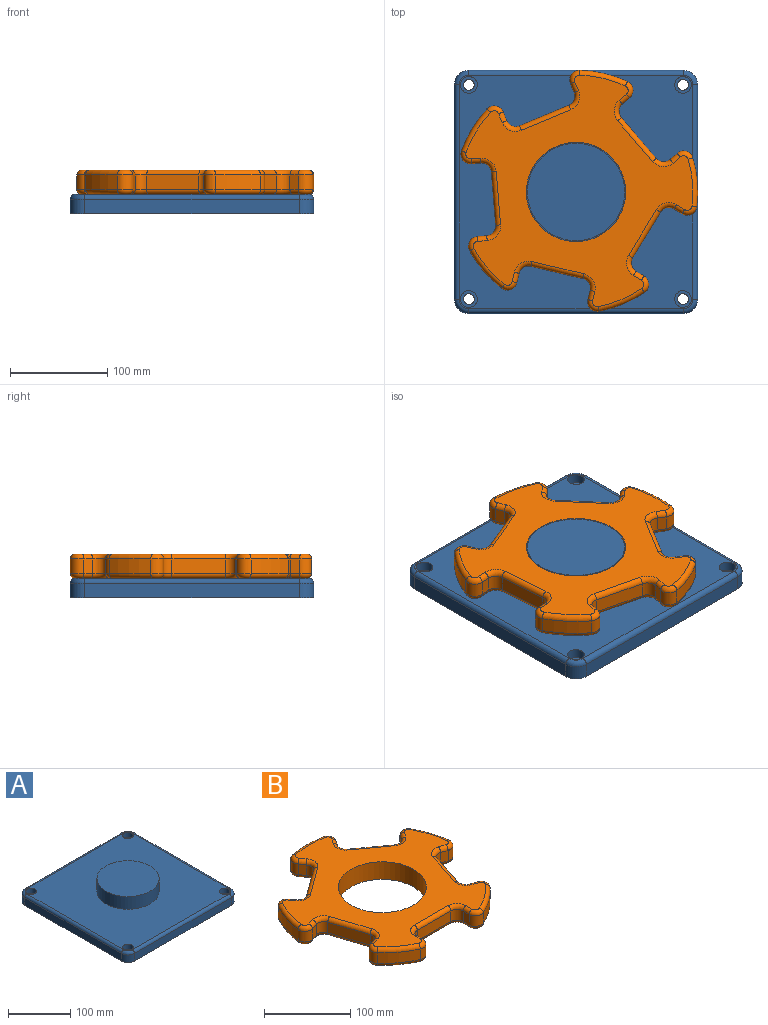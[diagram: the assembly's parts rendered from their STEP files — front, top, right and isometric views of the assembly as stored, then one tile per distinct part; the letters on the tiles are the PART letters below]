
ASSEMBLY  parts=2 mates=1
PART A: 32 faces, bbox 252.5x252.5x45 mm
  f0: plane 220x15mm, normal (1,0,0), area 3300mm2, adj f5,f8,f11,f27
  f1: plane 220x15mm, normal (0,1,0), area 3300mm2, adj f5,f8,f9,f31
  f2: plane 220x15mm, normal (-1,0,0), area 3300mm2, adj f5,f9,f10,f28
  f3: plane 220x15mm, normal (0,-1,0), area 3300mm2, adj f5,f10,f11,f24
  f4: plane 240x240mm, normal (0,0,1), area 48725.4mm2, adj f6,f14,f17,f20,f23,f24,f25,f26
  f5: plane 250x250mm, normal (0,0,-1), area 61926.7mm2, adj f0,f1,f2,f3,f8,f9,f10,f11
  f6: cylinder r=50mm len=100mm, axis (0,0,-1), area 7854mm2, adj f4,f7
  f7: plane 100x100mm, normal (0,0,1), area 7854mm2, adj f6
  f8: cylinder r=15mm len=15mm, axis (0,0,-1), area 353.4mm2, adj f0,f1,f5,f29
  f9: cylinder r=15mm len=15mm, axis (0,0,1), area 353.4mm2, adj f1,f2,f5,f30
  f10: cylinder r=15mm len=15mm, axis (0,0,-1), area 353.4mm2, adj f2,f3,f5,f26
  f11: cylinder r=15mm len=15mm, axis (0,0,1), area 353.4mm2, adj f0,f3,f5,f25
  f12: cylinder r=5.5mm len=11mm, axis (0,0,1), area 345.6mm2, adj f5,f13
  f13: plane 17.25x17.25mm, normal (0,0,1), area 138.7mm2, adj f12,f14
  f14: cylinder r=8.62mm len=17.25mm, axis (0,0,1), area 541.9mm2, adj f4,f13
  f15: cylinder r=5.5mm len=11mm, axis (0,0,1), area 345.6mm2, adj f5,f16
  f16: plane 17.25x17.25mm, normal (0,0,1), area 138.7mm2, adj f15,f17
  f17: cylinder r=8.62mm len=17.25mm, axis (0,0,1), area 541.9mm2, adj f4,f16
  f18: cylinder r=5.5mm len=11mm, axis (0,0,1), area 345.6mm2, adj f5,f19
  f19: plane 17.25x17.25mm, normal (0,0,1), area 138.7mm2, adj f18,f20
  f20: cylinder r=8.62mm len=17.25mm, axis (0,0,1), area 541.9mm2, adj f4,f19
  f21: cylinder r=5.5mm len=11mm, axis (0,0,1), area 345.6mm2, adj f5,f22
  f22: plane 17.25x17.25mm, normal (0,0,1), area 138.7mm2, adj f21,f23
  f23: cylinder r=8.62mm len=17.25mm, axis (0,0,1), area 541.9mm2, adj f4,f22
  f24: cylinder r=5mm len=220mm, axis (-1,0,0), area 1727.9mm2, adj f3,f4,f25,f26
  f25: torus R=10mm, axis (0,0,1), area 162.6mm2, adj f4,f11,f24,f27
  f26: torus R=10mm, axis (0,0,1), area 162.6mm2, adj f4,f10,f24,f28
  f27: cylinder r=5mm len=220mm, axis (0,-1,0), area 1727.9mm2, adj f0,f4,f25,f29
  f28: cylinder r=5mm len=220mm, axis (0,1,0), area 1727.9mm2, adj f2,f4,f26,f30
  f29: torus R=10mm, axis (0,0,1), area 162.6mm2, adj f4,f8,f27,f31
  f30: torus R=10mm, axis (0,0,1), area 162.6mm2, adj f4,f9,f28,f31
  f31: cylinder r=5mm len=220mm, axis (1,0,0), area 1727.9mm2, adj f1,f4,f29,f30
PART B: 123 faces, bbox 268.9x258.5x25 mm
  f0: plane 238.57x229.73mm, normal (0,0,1), area 21505.7mm2, adj f6,f43,f44,f45,f46,f47,f48,f49
  f1: plane 238.57x229.73mm, normal (0,0,-1), area 21505.7mm2, adj f6,f83,f84,f85,f86,f87,f88,f89
  f2: cylinder r=125mm len=40.68mm, axis (0,0,-1), area 759.5mm2, adj f13,f42,f51,f91
  f3: cylinder r=125mm len=47.82mm, axis (0,0,-1), area 759.5mm2, adj f35,f41,f67,f107
  f4: cylinder r=125mm len=50.29mm, axis (0,0,-1), area 759.5mm2, adj f28,f34,f82,f122
  f5: cylinder r=125mm len=47.82mm, axis (0,0,-1), area 759.5mm2, adj f21,f27,f66,f106
  f6: cylinder r=51mm len=102mm, axis (0,0,-1), area 8011.1mm2, adj f0,f1
  f7: cylinder r=125mm len=40.68mm, axis (0,0,-1), area 759.5mm2, adj f14,f20,f50,f90
  f8: plane 15x9.73mm, normal (-1,0,0), area 146mm2, adj f11,f14,f46,f86
  f9: plane 55x15mm, normal (0,-1,0), area 825mm2, adj f11,f12,f43,f83
  f10: plane 15x9.73mm, normal (1,0,0), area 146mm2, adj f12,f13,f47,f87
  f11: cylinder r=10mm len=15mm, axis (0,0,-1), area 235.6mm2, adj f8,f9,f44,f84
  f12: cylinder r=10mm len=15mm, axis (0,0,-1), area 235.6mm2, adj f9,f10,f45,f85
  f13: cylinder r=10mm len=15mm, axis (0,0,-1), area 299.5mm2, adj f2,f10,f49,f89
  f14: cylinder r=10mm len=15mm, axis (0,0,-1), area 299.5mm2, adj f7,f8,f48,f88
  f15: plane 15x9.26mm, normal (-0.31,-0.95,0), area 146mm2, adj f18,f21,f62,f102
  f16: plane 52.31x17mm, normal (0.95,-0.31,0), area 825mm2, adj f18,f19,f58,f98
  f17: plane 15x9.26mm, normal (0.31,0.95,0), area 146mm2, adj f19,f20,f54,f94
  f18: cylinder r=10mm len=15mm, axis (0,0,-1), area 235.6mm2, adj f15,f16,f60,f100
  f19: cylinder r=10mm len=15mm, axis (0,0,-1), area 235.6mm2, adj f16,f17,f56,f96
  f20: cylinder r=10mm len=16.25mm, axis (0,0,-1), area 299.5mm2, adj f7,f17,f52,f92
  f21: cylinder r=10mm len=15mm, axis (0,0,-1), area 299.5mm2, adj f5,f15,f64,f104
  f22: plane 15x7.87mm, normal (0.81,-0.59,0), area 146mm2, adj f25,f28,f78,f118
  f23: plane 44.5x32.33mm, normal (0.59,0.81,0), area 825mm2, adj f25,f26,f74,f114
  f24: plane 15x7.87mm, normal (-0.81,0.59,0), area 146mm2, adj f26,f27,f70,f110
  f25: cylinder r=10mm len=15mm, axis (0,0,-1), area 235.6mm2, adj f22,f23,f76,f116
  f26: cylinder r=10mm len=15mm, axis (0,0,-1), area 235.6mm2, adj f23,f24,f72,f112
  f27: cylinder r=10mm len=16.78mm, axis (0,0,-1), area 299.5mm2, adj f5,f24,f68,f108
  f28: cylinder r=10mm len=15.67mm, axis (0,0,-1), area 299.5mm2, adj f4,f22,f80,f120
  f29: plane 15x7.87mm, normal (0.81,0.59,0), area 146mm2, adj f32,f35,f71,f111
  f30: plane 44.5x32.33mm, normal (-0.59,0.81,0), area 825mm2, adj f32,f33,f75,f115
  f31: plane 15x7.87mm, normal (-0.81,-0.59,0), area 146mm2, adj f33,f34,f79,f119
  f32: cylinder r=10mm len=15mm, axis (0,0,-1), area 235.6mm2, adj f29,f30,f73,f113
  f33: cylinder r=10mm len=15mm, axis (0,0,-1), area 235.6mm2, adj f30,f31,f77,f117
  f34: cylinder r=10mm len=15.67mm, axis (0,0,-1), area 299.5mm2, adj f4,f31,f81,f121
  f35: cylinder r=10mm len=16.78mm, axis (0,0,-1), area 299.5mm2, adj f3,f29,f69,f109
  f36: plane 15x9.26mm, normal (-0.31,0.95,0), area 146mm2, adj f39,f42,f55,f95
  f37: plane 52.31x17mm, normal (-0.95,-0.31,0), area 825mm2, adj f39,f40,f59,f99
  f38: plane 15x9.26mm, normal (0.31,-0.95,0), area 146mm2, adj f40,f41,f63,f103
  f39: cylinder r=10mm len=15mm, axis (0,0,-1), area 235.6mm2, adj f36,f37,f57,f97
  f40: cylinder r=10mm len=15mm, axis (0,0,-1), area 235.6mm2, adj f37,f38,f61,f101
  f41: cylinder r=10mm len=15mm, axis (0,0,-1), area 299.5mm2, adj f3,f38,f65,f105
  f42: cylinder r=10mm len=16.25mm, axis (0,0,-1), area 299.5mm2, adj f2,f36,f53,f93
  f43: cylinder r=5mm len=55mm, axis (1,0,0), area 432mm2, adj f0,f9,f44,f45
  f44: torus R=15mm, axis (0,0,1), area 145.8mm2, adj f0,f11,f43,f46
  f45: torus R=15mm, axis (0,0,1), area 145.8mm2, adj f0,f12,f43,f47
  f46: cylinder r=5mm len=9.73mm, axis (0,-1,0), area 76.4mm2, adj f0,f8,f44,f48
  f47: cylinder r=5mm len=9.73mm, axis (0,1,0), area 76.4mm2, adj f0,f10,f45,f49
  f48: torus R=5mm, axis (0,0,1), area 128.3mm2, adj f0,f14,f46,f50
  f49: torus R=5mm, axis (0,0,1), area 128.3mm2, adj f0,f13,f47,f51
  f50: torus R=120mm, axis (0,0,1), area 391.9mm2, adj f0,f7,f48,f52
  f51: torus R=120mm, axis (0,0,1), area 391.9mm2, adj f0,f2,f49,f53
  f52: torus R=5mm, axis (0,0,1), area 128.3mm2, adj f0,f20,f50,f54
  f53: torus R=5mm, axis (0,0,1), area 128.3mm2, adj f0,f42,f51,f55
  f54: cylinder r=5mm len=10.8mm, axis (-0.95,0.31,0), area 76.4mm2, adj f0,f17,f52,f56
  f55: cylinder r=5mm len=10.8mm, axis (-0.95,-0.31,0), area 76.4mm2, adj f0,f36,f53,f57
  f56: torus R=15mm, axis (0,0,1), area 145.8mm2, adj f0,f19,f54,f58
  f57: torus R=15mm, axis (0,0,1), area 145.8mm2, adj f0,f39,f55,f59
  f58: cylinder r=5mm len=53.85mm, axis (0.31,0.95,0), area 432mm2, adj f0,f16,f56,f60
  f59: cylinder r=5mm len=53.85mm, axis (0.31,-0.95,0), area 432mm2, adj f0,f37,f57,f61
  f60: torus R=15mm, axis (0,0,1), area 145.8mm2, adj f0,f18,f58,f62
  f61: torus R=15mm, axis (0,0,1), area 145.8mm2, adj f0,f40,f59,f63
  f62: cylinder r=5mm len=10.8mm, axis (0.95,-0.31,0), area 76.4mm2, adj f0,f15,f60,f64
  f63: cylinder r=5mm len=10.8mm, axis (0.95,0.31,0), area 76.4mm2, adj f0,f38,f61,f65
  f64: torus R=5mm, axis (0,0,1), area 128.3mm2, adj f0,f21,f62,f66
  f65: torus R=5mm, axis (0,0,1), area 128.3mm2, adj f0,f41,f63,f67
  f66: torus R=120mm, axis (0,0,1), area 391.9mm2, adj f0,f5,f64,f68
  f67: torus R=120mm, axis (0,0,1), area 391.9mm2, adj f0,f3,f65,f69
  f68: torus R=5mm, axis (0,0,1), area 128.3mm2, adj f0,f27,f66,f70
  f69: torus R=5mm, axis (0,0,1), area 128.3mm2, adj f0,f35,f67,f71
  f70: cylinder r=5mm len=10.81mm, axis (-0.59,-0.81,0), area 76.4mm2, adj f0,f24,f68,f72
  f71: cylinder r=5mm len=10.81mm, axis (-0.59,0.81,0), area 76.4mm2, adj f0,f29,f69,f73
  f72: torus R=15mm, axis (0,0,1), area 145.8mm2, adj f0,f26,f70,f74
  f73: torus R=15mm, axis (0,0,1), area 145.8mm2, adj f0,f32,f71,f75
  f74: cylinder r=5mm len=47.44mm, axis (-0.81,0.59,0), area 432mm2, adj f0,f23,f72,f76
  f75: cylinder r=5mm len=47.44mm, axis (-0.81,-0.59,0), area 432mm2, adj f0,f30,f73,f77
  f76: torus R=15mm, axis (0,0,1), area 145.8mm2, adj f0,f25,f74,f78
  f77: torus R=15mm, axis (0,0,1), area 145.8mm2, adj f0,f33,f75,f79
  f78: cylinder r=5mm len=10.81mm, axis (0.59,0.81,0), area 76.4mm2, adj f0,f22,f76,f80
  f79: cylinder r=5mm len=10.81mm, axis (0.59,-0.81,0), area 76.4mm2, adj f0,f31,f77,f81
  f80: torus R=5mm, axis (0,0,1), area 128.3mm2, adj f0,f28,f78,f82
  f81: torus R=5mm, axis (0,0,1), area 128.3mm2, adj f0,f34,f79,f82
  f82: torus R=120mm, axis (0,0,1), area 391.9mm2, adj f0,f4,f80,f81
  f83: cylinder r=5mm len=55mm, axis (-1,0,0), area 432mm2, adj f1,f9,f84,f85
  f84: torus R=15mm, axis (0,0,1), area 145.8mm2, adj f1,f11,f83,f86
  f85: torus R=15mm, axis (0,0,1), area 145.8mm2, adj f1,f12,f83,f87
  f86: cylinder r=5mm len=9.73mm, axis (0,1,0), area 76.4mm2, adj f1,f8,f84,f88
  f87: cylinder r=5mm len=9.73mm, axis (0,-1,0), area 76.4mm2, adj f1,f10,f85,f89
  f88: torus R=5mm, axis (0,0,1), area 128.3mm2, adj f1,f14,f86,f90
  f89: torus R=5mm, axis (0,0,1), area 128.3mm2, adj f1,f13,f87,f91
  f90: torus R=120mm, axis (0,0,1), area 391.9mm2, adj f1,f7,f88,f92
  f91: torus R=120mm, axis (0,0,1), area 391.9mm2, adj f1,f2,f89,f93
  f92: torus R=5mm, axis (0,0,1), area 128.3mm2, adj f1,f20,f90,f94
  f93: torus R=5mm, axis (0,0,1), area 128.3mm2, adj f1,f42,f91,f95
  f94: cylinder r=5mm len=10.8mm, axis (0.95,-0.31,0), area 76.4mm2, adj f1,f17,f92,f96
  f95: cylinder r=5mm len=10.8mm, axis (0.95,0.31,0), area 76.4mm2, adj f1,f36,f93,f97
  f96: torus R=15mm, axis (0,0,1), area 145.8mm2, adj f1,f19,f94,f98
  f97: torus R=15mm, axis (0,0,1), area 145.8mm2, adj f1,f39,f95,f99
  f98: cylinder r=5mm len=53.85mm, axis (-0.31,-0.95,0), area 432mm2, adj f1,f16,f96,f100
  f99: cylinder r=5mm len=53.85mm, axis (-0.31,0.95,0), area 432mm2, adj f1,f37,f97,f101
  f100: torus R=15mm, axis (0,0,1), area 145.8mm2, adj f1,f18,f98,f102
  f101: torus R=15mm, axis (0,0,1), area 145.8mm2, adj f1,f40,f99,f103
  f102: cylinder r=5mm len=10.8mm, axis (-0.95,0.31,0), area 76.4mm2, adj f1,f15,f100,f104
  f103: cylinder r=5mm len=10.8mm, axis (-0.95,-0.31,0), area 76.4mm2, adj f1,f38,f101,f105
  f104: torus R=5mm, axis (0,0,1), area 128.3mm2, adj f1,f21,f102,f106
  f105: torus R=5mm, axis (0,0,1), area 128.3mm2, adj f1,f41,f103,f107
  f106: torus R=120mm, axis (0,0,1), area 391.9mm2, adj f1,f5,f104,f108
  f107: torus R=120mm, axis (0,0,1), area 391.9mm2, adj f1,f3,f105,f109
  f108: torus R=5mm, axis (0,0,1), area 128.3mm2, adj f1,f27,f106,f110
  f109: torus R=5mm, axis (0,0,1), area 128.3mm2, adj f1,f35,f107,f111
  f110: cylinder r=5mm len=10.81mm, axis (0.59,0.81,0), area 76.4mm2, adj f1,f24,f108,f112
  f111: cylinder r=5mm len=10.81mm, axis (0.59,-0.81,0), area 76.4mm2, adj f1,f29,f109,f113
  f112: torus R=15mm, axis (0,0,1), area 145.8mm2, adj f1,f26,f110,f114
  f113: torus R=15mm, axis (0,0,1), area 145.8mm2, adj f1,f32,f111,f115
  f114: cylinder r=5mm len=47.44mm, axis (0.81,-0.59,0), area 432mm2, adj f1,f23,f112,f116
  f115: cylinder r=5mm len=47.44mm, axis (0.81,0.59,0), area 432mm2, adj f1,f30,f113,f117
  f116: torus R=15mm, axis (0,0,1), area 145.8mm2, adj f1,f25,f114,f118
  f117: torus R=15mm, axis (0,0,1), area 145.8mm2, adj f1,f33,f115,f119
  f118: cylinder r=5mm len=10.81mm, axis (-0.59,-0.81,0), area 76.4mm2, adj f1,f22,f116,f120
  f119: cylinder r=5mm len=10.81mm, axis (-0.59,0.81,0), area 76.4mm2, adj f1,f31,f117,f121
  f120: torus R=5mm, axis (0,0,1), area 128.3mm2, adj f1,f28,f118,f122
  f121: torus R=5mm, axis (0,0,1), area 128.3mm2, adj f1,f34,f119,f122
  f122: torus R=120mm, axis (0,0,1), area 391.9mm2, adj f1,f4,f120,f121
PLACE A at identity fixed
PLACE B rot(axis=(0,0,-1),157.4deg) t=(0,0,0)mm
MATE revolute A.f6 <-> B.f2  axis (0,0,1) through (0,0,45)mm
